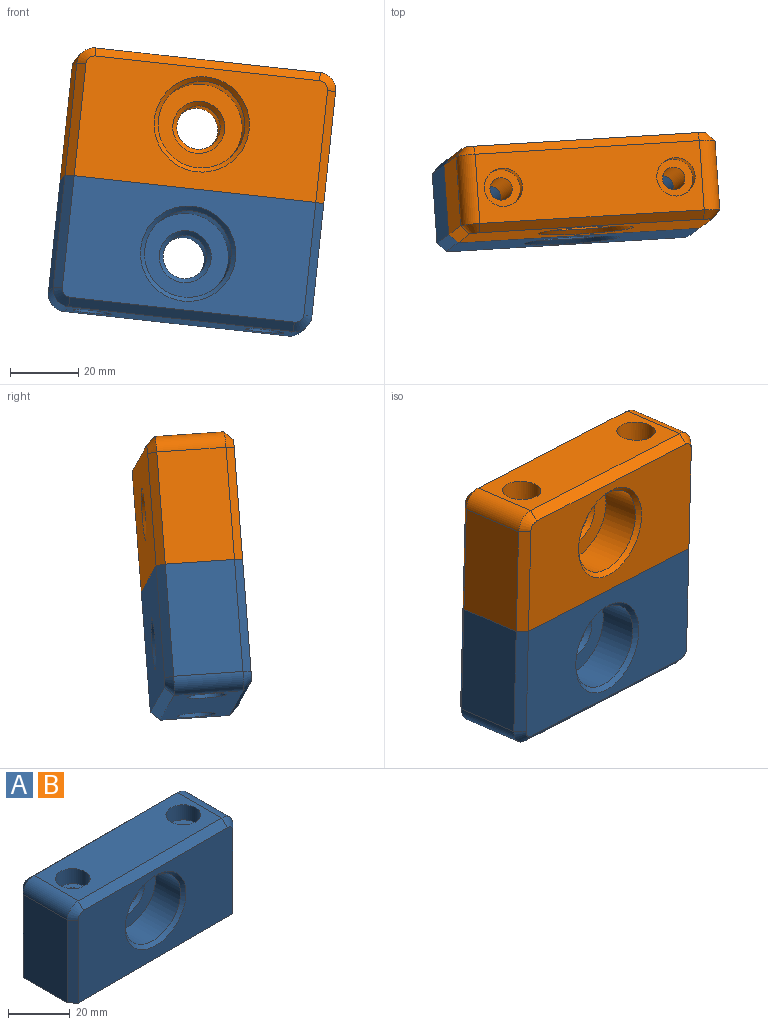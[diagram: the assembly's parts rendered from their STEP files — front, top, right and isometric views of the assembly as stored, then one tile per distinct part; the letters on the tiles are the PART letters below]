
ASSEMBLY  parts=2 mates=1
PART A: 30 faces, bbox 76.2x25.4x38.1 mm
  f0: plane 66.04x20.32mm, normal (0,0,1), area 1143.1mm2, adj f6,f7,f13,f16,f19,f24
  f1: plane 33.02x20.32mm, normal (-1,0,0), area 671mm2, adj f2,f6,f21,f26
  f2: plane 76.2x25.4mm, normal (0,0,-1), area 1854.2mm2, adj f1,f3,f4,f5,f11,f14,f17,f21
  f3: plane 33.02x20.32mm, normal (1,0,0), area 671mm2, adj f2,f7,f17,f22
  f4: plane 71.12x35.56mm, normal (0,-1,0), area 1913.1mm2, adj f2,f22,f23,f24,f25,f26,f27
  f5: plane 71.12x35.56mm, normal (0,1,0), area 2343.8mm2, adj f2,f17,f18,f19,f20,f21,f29
  f6: cylinder r=5.08mm len=20.32mm, axis (0,1,0), area 162.1mm2, adj f0,f1,f20,f25
  f7: cylinder r=5.08mm len=20.32mm, axis (0,-1,0), area 162.1mm2, adj f0,f3,f18,f23
  f8: cylinder r=12.7mm len=25.4mm, axis (0,-1,0), area 912.1mm2, adj f9,f27
  f9: plane 25.4x25.4mm, normal (0,-1,0), area 324.3mm2, adj f8,f28
  f10: cylinder r=6.35mm len=12.7mm, axis (0,-1,0), area 405.4mm2, adj f28,f29
  f11: cylinder r=3.3mm len=32.1mm, axis (0,0,1), area 665.6mm2, adj f2,f12
  f12: plane 11.25x11.25mm, normal (0,0,1), area 65.2mm2, adj f11,f13
  f13: cylinder r=5.62mm len=11.25mm, axis (0,0,1), area 212.1mm2, adj f0,f12
  f14: cylinder r=3.3mm len=32.1mm, axis (0,0,1), area 665.6mm2, adj f2,f15
  f15: plane 11.25x11.25mm, normal (0,0,1), area 65.2mm2, adj f14,f16
  f16: cylinder r=5.62mm len=11.25mm, axis (0,0,1), area 212.1mm2, adj f0,f15
  f17: plane 33.02x2.54mm, normal (0.71,0.71,0), area 118.6mm2, adj f2,f3,f5,f18
  f18: cone r=2.54mm half-angle=45deg, axis (0,-1,0), area 21.5mm2, adj f5,f7,f17,f19
  f19: plane 66.04x2.54mm, normal (0,0.71,0.71), area 237.2mm2, adj f0,f5,f18,f20
  f20: cone r=2.54mm half-angle=45deg, axis (0,-1,0), area 21.5mm2, adj f5,f6,f19,f21
  f21: plane 33.02x2.54mm, normal (-0.71,0.71,0), area 118.6mm2, adj f1,f2,f5,f20
  f22: plane 33.02x2.54mm, normal (0.71,-0.71,0), area 118.6mm2, adj f2,f3,f4,f23
  f23: cone r=2.54mm half-angle=45deg, axis (0,1,0), area 21.5mm2, adj f4,f7,f22,f24
  f24: plane 66.04x2.54mm, normal (0,-0.71,0.71), area 237.2mm2, adj f0,f4,f23,f25
  f25: cone r=2.54mm half-angle=45deg, axis (0,1,0), area 21.5mm2, adj f4,f6,f24,f26
  f26: plane 33.02x2.54mm, normal (-0.71,-0.71,0), area 118.6mm2, adj f1,f2,f4,f25
  f27: cone r=12.7mm half-angle=45deg, axis (0,-1,0), area 150.5mm2, adj f4,f8
  f28: cone r=6.35mm half-angle=45deg, axis (0,-1,0), area 78.8mm2, adj f9,f10
  f29: cone r=7.62mm half-angle=45deg, axis (0,1,0), area 78.8mm2, adj f5,f10
PART B: same geometry as A
PLACE A rot(axis=(0.03,-1,0.04),173.9deg) t=(29.55,53.26,-53.45)mm
PLACE B rot(axis=(-0.5,0.74,0.45),8.3deg) t=(-46.06,48.66,-45.13)mm
MATE fastened B.f11 <-> A.f14  axis (-0.1,-0.07,-0.99) through (-32.59,36.79,-45.65)mm
